# Revit family: HERZ-Mini-D-Design-Thermostatic Sensor with snap fastener M28x2.0 9200 09
name_source: partatom
category: Rohrzubehör
units: mm (PartAtom-declared; Revit-internal decimal feet)

## family parameters
Arbeitsebenenbasiert = Nein
Beim Laden mit Abzugskörper schneiden = Nein
Bemaßung runder Anschluss = Durchmesser verwenden
Gemeinsam genutzt = Nein
Immer vertikal = Nein
OmniClass-Nummer = 23.65.55.14
OmniClass-Titel = Valves for Liquid Services
Teiletyp = Normal

## types (1)
- HERZ-Mini-D-Design-Thermostatic Sensor with snap fastener M28x2.0 9200 09
    Application = Central of heating usind the room.
    Frost protection = 6°C
    Hand wheel = plastic, white
    Hersteller = HERZ Armaturen Ges.m.b.H.
    LO1 = 5.5 mm  [stored 0.0180446 ft]
    LO2 = 18.6 mm  [stored 0.0610236 ft]
    Model = HERZ-design-thermostatic head MINI „D“,with liquid sensor (hydro sensor).
Only in combination with valve radiators (e.g. Vogel & Noot) appropriated.
Colour: white
    Operation = The HERZ-thermostat serves as a sensor and control element.
The change in volume of the liquid contained in the HERZ-hyrosensor actuates the valve spindle.
    Part number = 1920009
    S01 = 91.7 mm  [stored 0.300853 ft]
    S02 = 60 mm  [stored 0.19685 ft]
    Set value range = 0-30°C
    URL = www.herzvalves.com

note: [stored X ft] marks values corroborated as IEEE doubles in the binary element streams (Revit-internal decimal feet)
